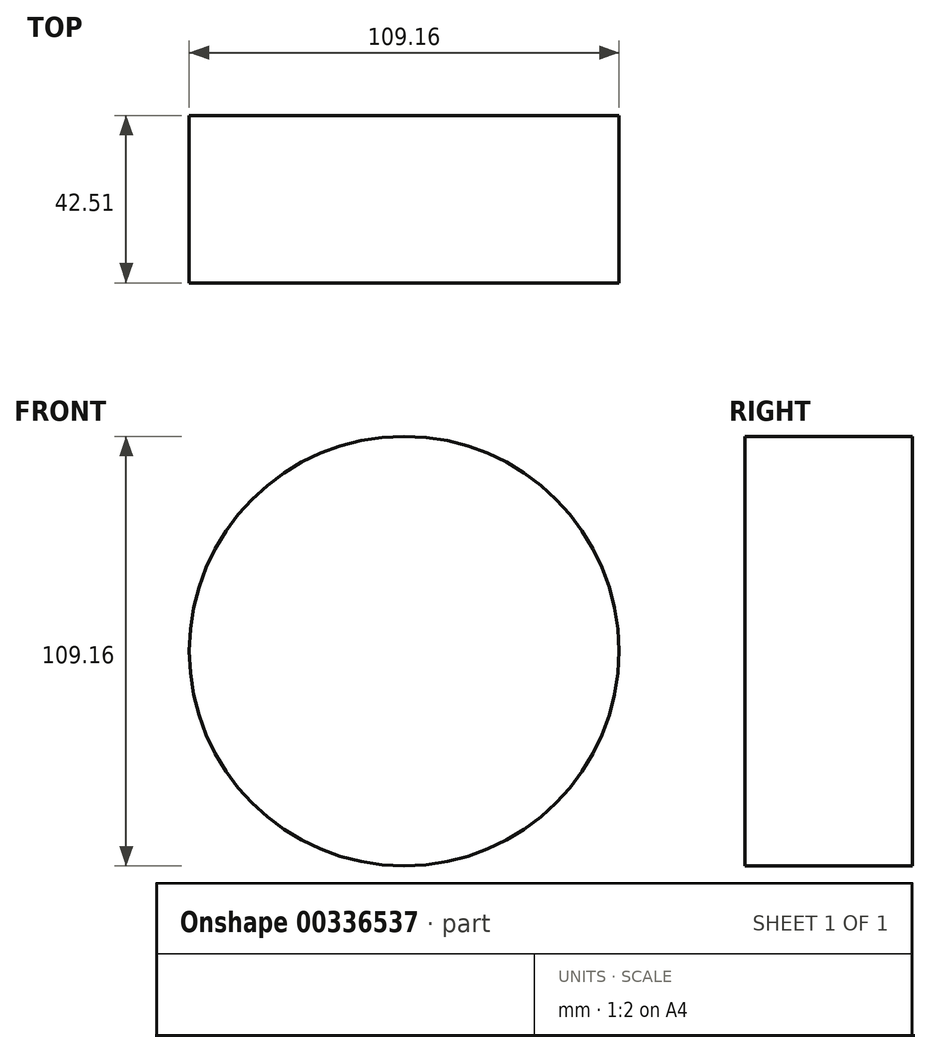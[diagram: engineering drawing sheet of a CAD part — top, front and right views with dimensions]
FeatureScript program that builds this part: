
annotation { "Feature Type Name" : "Feature", "Feature Type Description" : "" }
export const myFeature = defineFeature(function(context is Context, id is Id, definition is map)
    precondition{}
    {
        {
            var Q0;
            Q0=qCreatedBy(makeId("Front.planeOp"),FACE);
            var sketch = newSketch(context, id + "F0", { "sketchPlane" : qUnion([Q0])});
            skCircle(sketch, "E0", {"center": v(0, 0) * mm, "radius": 54.58 * mm});
            skSolve(sketch);
        }
        {
            var Q0;
            Q0=makeQuery(id+"F0.imprint","IMPRINT",FACE,{"disambiguationData":[TD([[makeQuery(id+"F0.imprint","IMPRINT",EDGE,{"derivedFrom":sQuery(id+"F0.wireOp",EDGE,"E0")}),1.0]])]});
            extrude(context, id + "F1", {"entities" : qUnion([Q0]), "depth" : 42.5 * mm});
        }
    });
